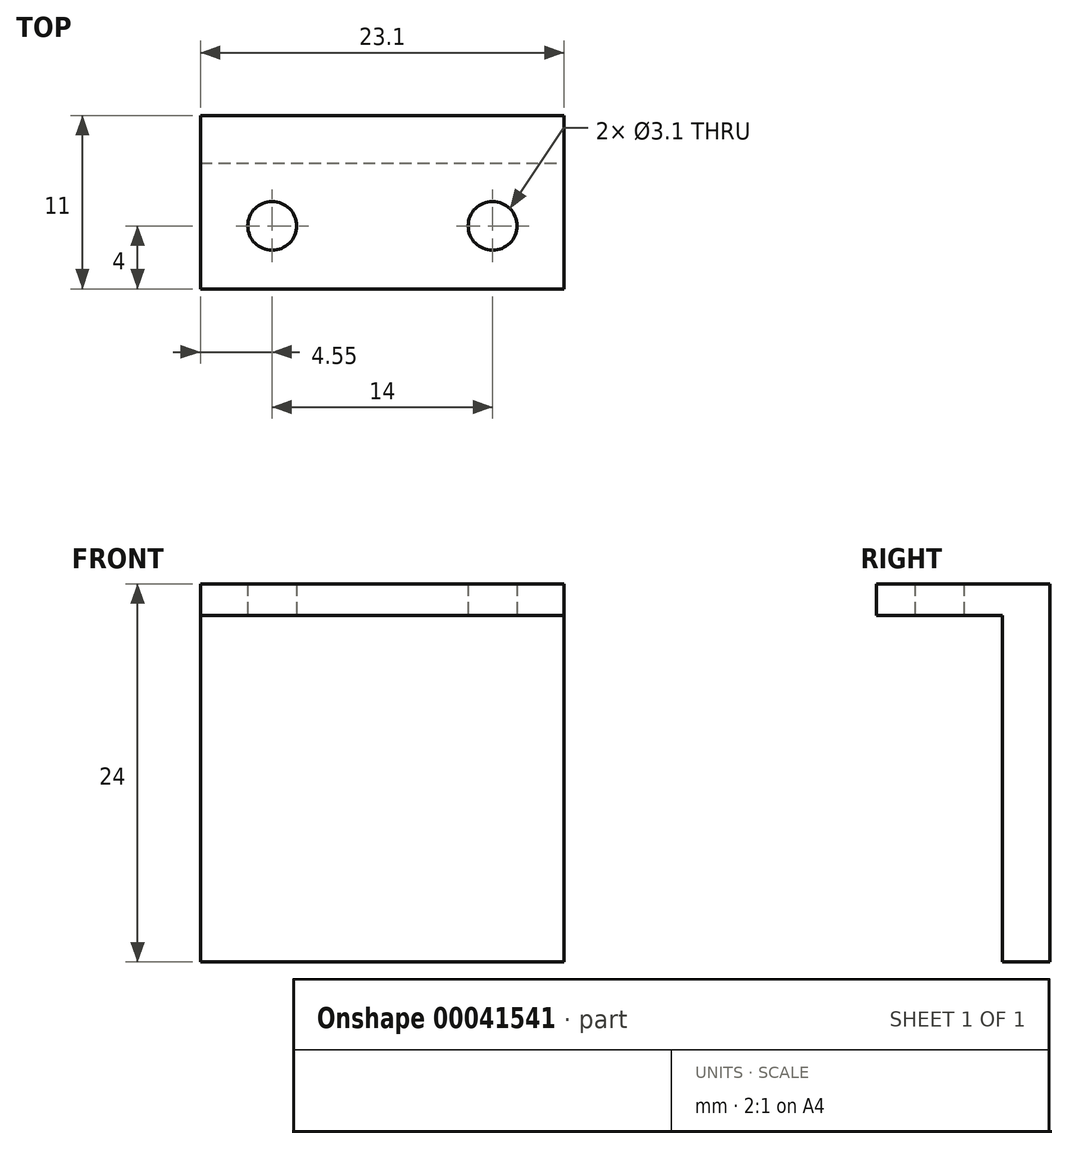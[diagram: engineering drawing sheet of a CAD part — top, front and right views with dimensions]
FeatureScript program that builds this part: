
annotation { "Feature Type Name" : "Feature", "Feature Type Description" : "" }
export const myFeature = defineFeature(function(context is Context, id is Id, definition is map)
    precondition{}
    {
        {
            var Q0;
            Q0=qCreatedBy(makeId("Top.planeOp"),FACE);
            var sketch = newSketch(context, id + "F0", { "sketchPlane" : qUnion([Q0])});
            skLineSegment(sketch, "E0.rect.bottom", {"start": v(11.55, -4) * mm, "end": v(-11.55, -4) * mm});
            skLineSegment(sketch, "E0.rect.top", {"start": v(11.55, 4) * mm, "end": v(-11.55, 4) * mm});
            skLineSegment(sketch, "E0.rect.left", {"start": v(11.55, -4) * mm, "end": v(11.55, 4) * mm});
            skLineSegment(sketch, "E0.rect.right", {"start": v(-11.55, -4) * mm, "end": v(-11.55, 4) * mm});
            skPoint(sketch, "E0.rect.middle", {"position": v(0, 0) * mm});
            skCircle(sketch, "E1", {"center": v(-7, 0) * mm, "radius": 1.55 * mm});
            skCircle(sketch, "E2", {"center": v(7, 0) * mm, "radius": 1.55 * mm});
            skLineSegment(sketch, "E3", {"start": v(0, 0) * mm, "end": v(7, 0) * mm, "construction": true});
            skLineSegment(sketch, "E4", {"start": v(-7, 0) * mm, "end": v(0, 0) * mm, "construction": true});
            skLineSegment(sketch, "E5.bottom", {"start": v(-11.55, 4) * mm, "end": v(11.55, 4) * mm});
            skLineSegment(sketch, "E5.top", {"start": v(-11.55, 7) * mm, "end": v(11.55, 7) * mm});
            skLineSegment(sketch, "E5.left", {"start": v(-11.55, 4) * mm, "end": v(-11.55, 7) * mm});
            skLineSegment(sketch, "E5.right", {"start": v(11.55, 4) * mm, "end": v(11.55, 7) * mm});
            skSolve(sketch);
        }
        {
            var Q0;
            Q0 = qSketchRegion(id + "F0", true);
            extrude(context, id + "F1", {"entities" : qUnion([Q0]), "depth" : 2 * mm});
        }
        {
            var Q0;
            Q0=makeQuery(id+"F1.opExtrude","CAP_FACE",FACE,{"disambiguationData":[OSD([sQuery(id+"F0.wireOp",EDGE,"E0.rect.bottom"),sQuery(id+"F0.wireOp",EDGE,"E0.rect.left"),sQuery(id+"F0.wireOp",EDGE,"E0.rect.right"),sQuery(id+"F0.wireOp",EDGE,"E1"),sQuery(id+"F0.wireOp",EDGE,"E2"),sQuery(id+"F0.wireOp",EDGE,"E5.top"),sQuery(id+"F0.wireOp",EDGE,"E5.left"),sQuery(id+"F0.wireOp",EDGE,"E5.right")])],"isStart":true});
            var sketch = newSketch(context, id + "F2", { "sketchPlane" : qUnion([Q0])});
            skLineSegment(sketch, "E6.0", {"start": v(-11.55, -4) * mm, "end": v(11.55, -4) * mm});
            skLineSegment(sketch, "E7", {"start": v(11.55, -4) * mm, "end": v(11.55, -7) * mm});
            skLineSegment(sketch, "E8", {"start": v(11.55, -7) * mm, "end": v(-11.55, -7) * mm});
            skLineSegment(sketch, "E9", {"start": v(-11.55, -7) * mm, "end": v(-11.55, -4) * mm});
            skSolve(sketch);
        }
        {
            var Q0;
            Q0 = qSketchRegion(id + "F2", true);
            extrude(context, id + "F3", {"entities" : qUnion([Q0]), "operationType" : NewBodyOperationType.ADD, "depth" : 22 * mm});
        }
    });
